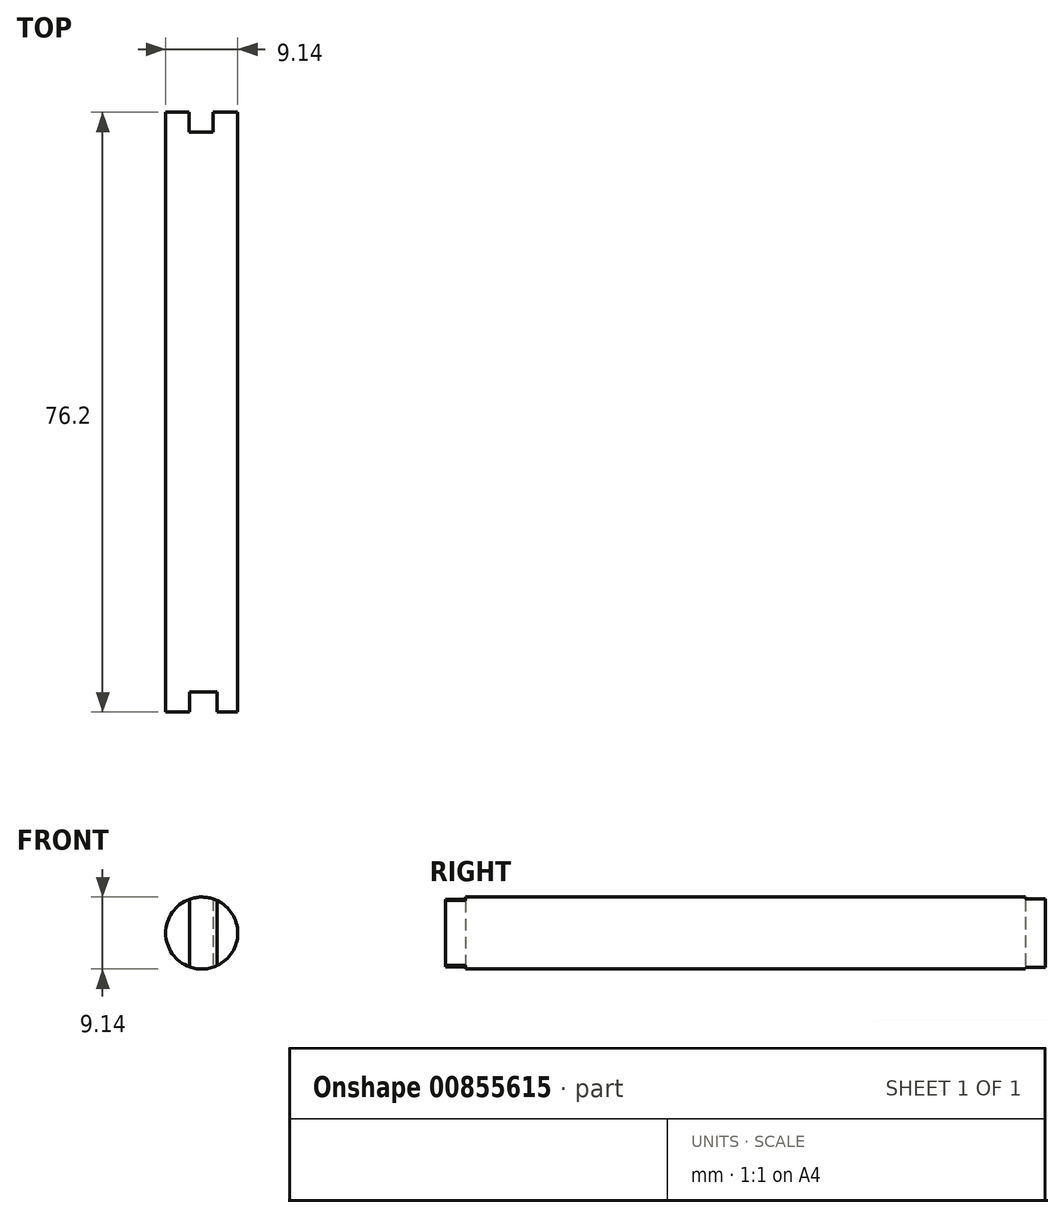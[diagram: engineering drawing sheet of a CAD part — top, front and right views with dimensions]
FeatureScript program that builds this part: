
annotation { "Feature Type Name" : "Feature", "Feature Type Description" : "" }
export const myFeature = defineFeature(function(context is Context, id is Id, definition is map)
    precondition{}
    {
        {
            var Q0;
            Q0=qCreatedBy(makeId("Front.planeOp"),FACE);
            var sketch = newSketch(context, id + "F0", { "sketchPlane" : qUnion([Q0])});
            skCircle(sketch, "E0", {"center": v(0, 0) * mm, "radius": 4.57 * mm});
            skSolve(sketch);
        }
        {
            var Q0;
            Q0=makeQuery(id+"F0.imprint","IMPRINT",FACE,{"disambiguationData":[TD([[makeQuery(id+"F0.imprint","IMPRINT",EDGE,{"derivedFrom":sQuery(id+"F0.wireOp",EDGE,"E0")}),1.0]])]});
            extrude(context, id + "F1", {"entities" : qUnion([Q0]), "depth" : 76.2 * mm, "offsetDistance" : 25.4 * mm});
        }
        {
            var Q0;
            Q0=makeQuery(id+"F1.opExtrude","CAP_FACE",FACE,{"disambiguationData":[OSD([sQuery(id+"F0.wireOp",EDGE,"E0")])],"isStart":false});
            var sketch = newSketch(context, id + "F2", { "sketchPlane" : qUnion([Q0])});
            skLineSegment(sketch, "E1.bottom", {"start": v(-1.55, 8.1) * mm, "end": v(1.97, 8.1) * mm});
            skLineSegment(sketch, "E1.top", {"start": v(-1.55, -7.66) * mm, "end": v(1.97, -7.66) * mm});
            skLineSegment(sketch, "E1.left", {"start": v(-1.55, 8.1) * mm, "end": v(-1.55, -7.66) * mm});
            skLineSegment(sketch, "E1.right", {"start": v(1.97, 8.1) * mm, "end": v(1.97, -7.66) * mm});
            skSolve(sketch);
        }
        {
            var Q0;
            {var subQ0=sQuery(id+"F2.wireOp",EDGE,"E1.bottom");Q0=makeQuery(id+"F2.imprint","IMPRINT",FACE,{"disambiguationData":[TD([[makeQuery(id+"F2.imprint","IMPRINT",EDGE,{"derivedFrom":subQ0}),-1.0]])]});}
            var Q1;
            {var subQ0=sQuery(id+"F2.wireOp",EDGE,"E1.top");Q1=makeQuery(id+"F2.imprint","IMPRINT",FACE,{"disambiguationData":[TD([[makeQuery(id+"F2.imprint","IMPRINT",EDGE,{"derivedFrom":subQ0}),1.0]])]});}
            var Q2;
            {var subQ0=sQuery(id+"F2.wireOp",EDGE,"E1.left");var subQ1=makeQuery(id+"F1.opExtrude","CAP_EDGE",EDGE,{"disambiguationData":[OSD([sQuery(id+"F0.wireOp",EDGE,"E0")])],"isStart":false});var subQ2=makeQuery(id+"F2.imprint","INTERSECT",VERTEX,{"disambiguationData":[OD(0.0)],"derivedFrom":[subQ1,subQ0]});Q2=makeQuery(id+"F2.imprint","IMPRINT",FACE,{"disambiguationData":[TD([[makeQuery(id+"F2.imprint","IMPRINT",EDGE,{"disambiguationData":[TD([[subQ2,-1.0]])],"derivedFrom":subQ0}),1.0]])]});}
            extrude(context, id + "F3", {"entities" : qUnion([Q0, Q1, Q2]), "operationType" : NewBodyOperationType.REMOVE, "oppositeDirection" : true, "depth" : 2.54 * mm, "offsetDistance" : 25.4 * mm});
        }
        {
            var Q0;
            Q0=makeQuery(id+"F1.opExtrude","CAP_FACE",FACE,{"disambiguationData":[OSD([sQuery(id+"F0.wireOp",EDGE,"E0")])],"isStart":true});
            var sketch = newSketch(context, id + "F4", { "sketchPlane" : qUnion([Q0])});
            skLineSegment(sketch, "E2.bottom", {"start": v(-1.45, 6.73) * mm, "end": v(1.6, 6.73) * mm});
            skLineSegment(sketch, "E2.top", {"start": v(-1.45, -7.65) * mm, "end": v(1.6, -7.65) * mm});
            skLineSegment(sketch, "E2.left", {"start": v(-1.45, 6.73) * mm, "end": v(-1.45, -7.65) * mm});
            skLineSegment(sketch, "E2.right", {"start": v(1.6, 6.73) * mm, "end": v(1.6, -7.65) * mm});
            skSolve(sketch);
        }
        {
            var Q0;
            {var subQ0=sQuery(id+"F4.wireOp",EDGE,"E2.left");var subQ1=makeQuery(id+"F1.opExtrude","CAP_EDGE",EDGE,{"disambiguationData":[OSD([sQuery(id+"F0.wireOp",EDGE,"E0")])],"isStart":true});var subQ2=makeQuery(id+"F4.imprint","INTERSECT",VERTEX,{"disambiguationData":[OD(0.0)],"derivedFrom":[subQ1,subQ0]});Q0=makeQuery(id+"F4.imprint","IMPRINT",FACE,{"disambiguationData":[TD([[makeQuery(id+"F4.imprint","IMPRINT",EDGE,{"disambiguationData":[TD([[subQ2,-1.0]])],"derivedFrom":subQ0}),1.0]])]});}
            extrude(context, id + "F5", {"entities" : qUnion([Q0]), "operationType" : NewBodyOperationType.REMOVE, "oppositeDirection" : true, "depth" : 2.54 * mm, "offsetDistance" : 25.4 * mm});
        }
    });
